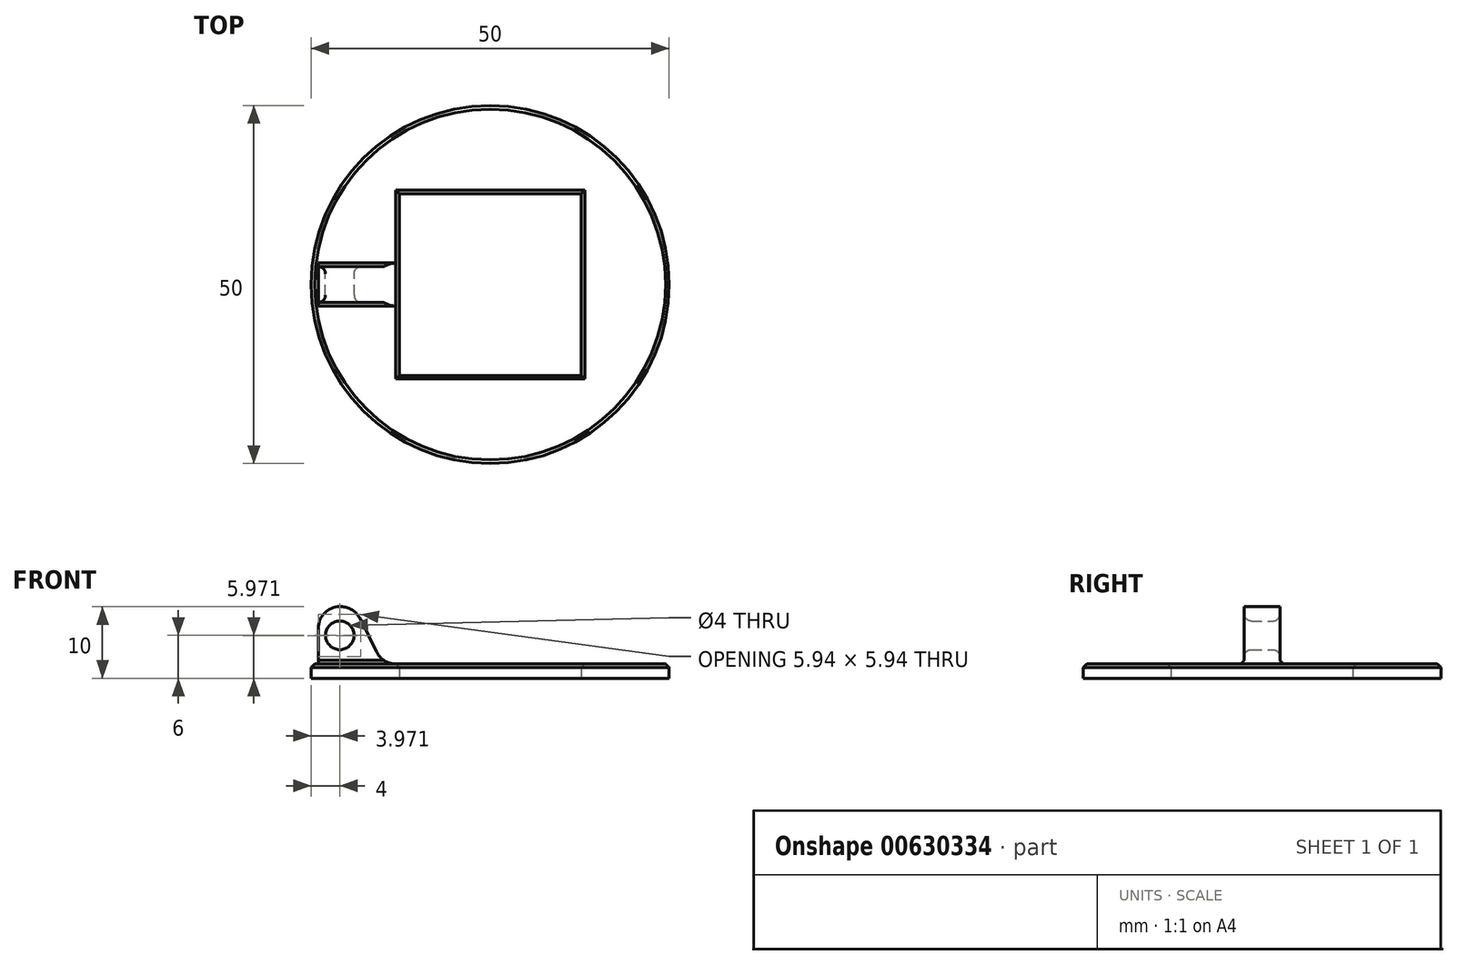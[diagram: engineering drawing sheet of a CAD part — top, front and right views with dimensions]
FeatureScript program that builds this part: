
annotation { "Feature Type Name" : "Feature", "Feature Type Description" : "" }
export const myFeature = defineFeature(function(context is Context, id is Id, definition is map)
    precondition{}
    {
        {
            var Q0;
            Q0=qCreatedBy(makeId("Top.planeOp"),FACE);
            var sketch = newSketch(context, id + "F0", { "sketchPlane" : qUnion([Q0])});
            skLineSegment(sketch, "E0.bottom", {"start": v(-12.7, 12.7) * mm, "end": v(12.7, 12.7) * mm});
            skLineSegment(sketch, "E0.top", {"start": v(-12.7, -12.7) * mm, "end": v(12.7, -12.7) * mm});
            skLineSegment(sketch, "E0.left", {"start": v(-12.7, 12.7) * mm, "end": v(-12.7, -12.7) * mm});
            skLineSegment(sketch, "E0.right", {"start": v(12.7, 12.7) * mm, "end": v(12.7, -12.7) * mm});
            skPoint(sketch, "E0.middle", {"position": v(0, 0) * mm});
            skCircle(sketch, "E1", {"center": v(0, 0) * mm, "radius": 25 * mm});
            skSolve(sketch);
        }
        {
            var Q0;
            Q0=makeQuery(id+"F0.imprint","IMPRINT",FACE,{"disambiguationData":[TD([[makeQuery(id+"F0.imprint","IMPRINT",EDGE,{"derivedFrom":sQuery(id+"F0.wireOp",EDGE,"E0.bottom")}),1.0]])]});
            extrude(context, id + "F1", {"entities" : qUnion([Q0]), "depth" : 2 * mm, "offsetDistance" : 25 * mm});
        }
        {
            var Q0;
            Q0=qCreatedBy(makeId("Front.planeOp"),FACE);
            var sketch = newSketch(context, id + "F2", { "sketchPlane" : qUnion([Q0])});
            skLineSegment(sketch, "E2", {"start": v(0, 0) * mm, "end": v(-24, 0) * mm});
            skLineSegment(sketch, "E3", {"start": v(-24, 0) * mm, "end": v(-24, 10) * mm});
            skLineSegment(sketch, "E4", {"start": v(-24, 10) * mm, "end": v(-19, 10) * mm});
            skLineSegment(sketch, "E5", {"start": v(-19, 10) * mm, "end": v(-14.73, 1.4) * mm});
            skLineSegment(sketch, "E6", {"start": v(-14.73, 1.4) * mm, "end": v(-24, 1.4) * mm});
            skLineSegment(sketch, "E7", {"start": v(-24, 10) * mm, "end": v(-24, 6) * mm, "construction": true});
            skLineSegment(sketch, "E8", {"start": v(-24, 6) * mm, "end": v(-21, 6) * mm, "construction": true});
            skCircle(sketch, "E9", {"center": v(-21, 6) * mm, "radius": 2 * mm});
            skSolve(sketch);
        }
        {
            var Q0;
            {var subQ0=sQuery(id+"F2.wireOp",EDGE,"E4");Q0=makeQuery(id+"F2.imprint","IMPRINT",FACE,{"disambiguationData":[TD([[makeQuery(id+"F2.imprint","IMPRINT",EDGE,{"derivedFrom":subQ0}),-1.0]])]});}
            extrude(context, id + "F3", {"entities" : qUnion([Q0]), "operationType" : NewBodyOperationType.ADD, "depth" : 2.5 * mm, "offsetDistance" : 25 * mm, "hasSecondDirection" : true, "secondDirectionOppositeDirection" : true, "secondDirectionDepth" : 2.5 * mm});
        }
        {
            var Q0;
            Q0=makeQuery(id+"F1.opExtrude","CAP_EDGE",EDGE,{"disambiguationData":[OSD([sQuery(id+"F0.wireOp",EDGE,"E0.bottom")])],"isStart":false});
            var Q1;
            Q1=makeQuery(id+"F1.opExtrude","CAP_EDGE",EDGE,{"disambiguationData":[OSD([sQuery(id+"F0.wireOp",EDGE,"E0.right")])],"isStart":false});
            var Q2;
            Q2=makeQuery(id+"F1.opExtrude","CAP_EDGE",EDGE,{"disambiguationData":[OSD([sQuery(id+"F0.wireOp",EDGE,"E0.top")])],"isStart":false});
            var Q3;
            Q3=makeQuery(id+"F1.opExtrude","CAP_EDGE",EDGE,{"disambiguationData":[OSD([sQuery(id+"F0.wireOp",EDGE,"E0.left")])],"isStart":false});
            var Q4;
            Q4=makeQuery(id+"F1.opExtrude","CAP_EDGE",EDGE,{"disambiguationData":[OSD([sQuery(id+"F0.wireOp",EDGE,"E1")])],"isStart":false});
            var Q5;
            Q5=makeQuery(id+"F3.boolean.opBoolean","INTERSECT",EDGE,{"derivedFrom":[makeQuery(id+"F1.opExtrude","CAP_FACE",FACE,{"disambiguationData":[OSD([sQuery(id+"F0.wireOp",EDGE,"E0.bottom"),sQuery(id+"F0.wireOp",EDGE,"E0.top"),sQuery(id+"F0.wireOp",EDGE,"E0.left"),sQuery(id+"F0.wireOp",EDGE,"E0.right"),sQuery(id+"F0.wireOp",EDGE,"E1")])],"isStart":false}),makeQuery(id+"F3.opExtrude","CAP_FACE",FACE,{"disambiguationData":[OSD([sQuery(id+"F2.wireOp",EDGE,"E3"),sQuery(id+"F2.wireOp",EDGE,"E4"),sQuery(id+"F2.wireOp",EDGE,"E5"),sQuery(id+"F2.wireOp",EDGE,"E6")])],"isStart":true})]});
            var Q6;
            Q6=makeQuery(id+"F3.boolean.opBoolean","INTERSECT",EDGE,{"derivedFrom":[makeQuery(id+"F1.opExtrude","CAP_FACE",FACE,{"disambiguationData":[OSD([sQuery(id+"F0.wireOp",EDGE,"E0.bottom"),sQuery(id+"F0.wireOp",EDGE,"E0.top"),sQuery(id+"F0.wireOp",EDGE,"E0.left"),sQuery(id+"F0.wireOp",EDGE,"E0.right"),sQuery(id+"F0.wireOp",EDGE,"E1")])],"isStart":false}),makeQuery(id+"F3.opExtrude","CAP_FACE",FACE,{"disambiguationData":[OSD([sQuery(id+"F2.wireOp",EDGE,"E3"),sQuery(id+"F2.wireOp",EDGE,"E4"),sQuery(id+"F2.wireOp",EDGE,"E5"),sQuery(id+"F2.wireOp",EDGE,"E6")])],"isStart":false})]});
            chamfer(context, id + "F4", {"entities" : qUnion([Q0, Q1, Q2, Q3, Q4, Q5, Q6]), "width" : .5 * mm, "tangentPropagation" : true});
        }
        {
            var Q0;
            Q0=makeQuery(id+"F3.opExtrude","CAP_EDGE",EDGE,{"disambiguationData":[OSD([sQuery(id+"F2.wireOp",EDGE,"E9")])],"isStart":false});
            var Q1;
            Q1=makeQuery(id+"F3.opExtrude","CAP_EDGE",EDGE,{"disambiguationData":[OSD([sQuery(id+"F2.wireOp",EDGE,"E9")])],"isStart":true});
            fillet(context, id + "F5", {"entities" : qUnion([Q0, Q1]), "radius" : 1 * mm, "tangentPropagation" : true, "allowEdgeOverflow" : false});
        }
        {
            var Q0;
            Q0=makeQuery(id+"F3.boolean.opBoolean","INTERSECT",EDGE,{"derivedFrom":[makeQuery(id+"F1.opExtrude","CAP_FACE",FACE,{"disambiguationData":[OSD([sQuery(id+"F0.wireOp",EDGE,"E0.bottom"),sQuery(id+"F0.wireOp",EDGE,"E0.top"),sQuery(id+"F0.wireOp",EDGE,"E0.left"),sQuery(id+"F0.wireOp",EDGE,"E0.right"),sQuery(id+"F0.wireOp",EDGE,"E1")])],"isStart":false}),makeQuery(id+"F3.opExtrude","SWEPT_FACE",FACE,{"disambiguationData":[OSD([sQuery(id+"F2.wireOp",EDGE,"E5")])]})]});
            var Q1;
            Q1=makeQuery(id+"F3.opExtrude","SWEPT_EDGE",EDGE,{"disambiguationData":[OSD([sQuery(id+"F2.wireOp",EDGE,"E3"),sQuery(id+"F2.wireOp",EDGE,"E4")])]});
            var Q2;
            Q2=makeQuery(id+"F3.opExtrude","SWEPT_EDGE",EDGE,{"disambiguationData":[OSD([sQuery(id+"F2.wireOp",EDGE,"E4"),sQuery(id+"F2.wireOp",EDGE,"E5")])]});
            fillet(context, id + "F6", {"entities" : qUnion([Q0, Q1, Q2]), "radius" : 3 * mm, "tangentPropagation" : true, "allowEdgeOverflow" : false});
        }
    });
